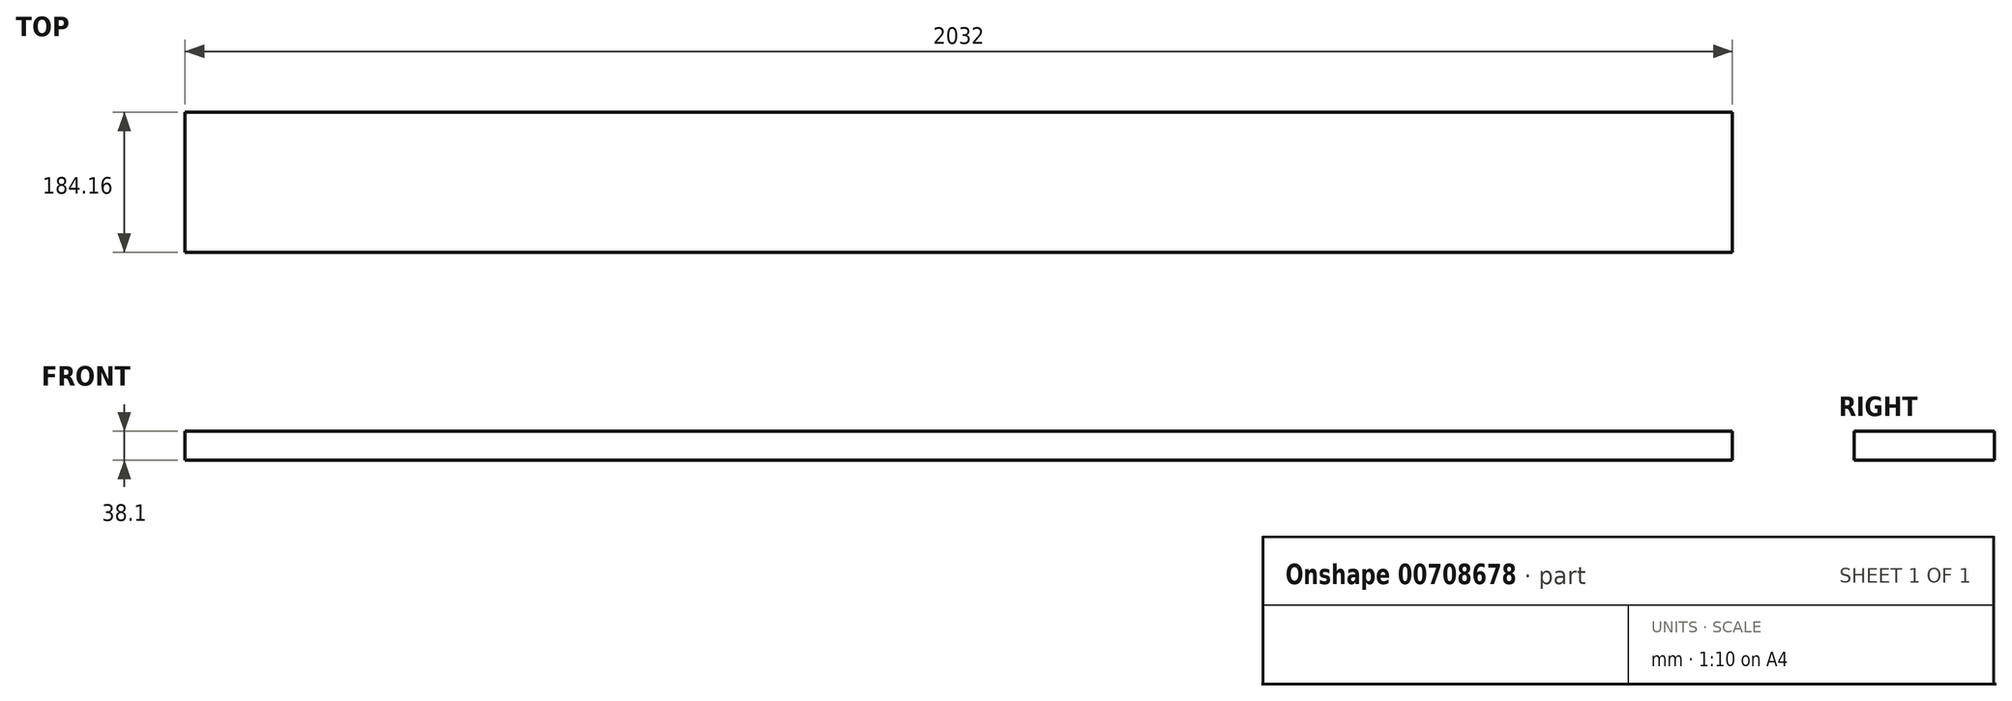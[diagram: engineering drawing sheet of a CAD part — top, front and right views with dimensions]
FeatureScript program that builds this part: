
annotation { "Feature Type Name" : "Feature", "Feature Type Description" : "" }
export const myFeature = defineFeature(function(context is Context, id is Id, definition is map)
    precondition{}
    {
        {
            var Q0;
            Q0=qCreatedBy(makeId("Right.planeOp"),FACE);
            var sketch = newSketch(context, id + "F0", { "sketchPlane" : qUnion([Q0])});
            skLineSegment(sketch, "E0.bottom", {"start": v(92.07, -19.05) * mm, "end": v(-92.07, -19.05) * mm});
            skLineSegment(sketch, "E0.top", {"start": v(92.07, 19.05) * mm, "end": v(-92.07, 19.05) * mm});
            skLineSegment(sketch, "E0.left", {"start": v(92.07, -19.05) * mm, "end": v(92.07, 19.05) * mm});
            skLineSegment(sketch, "E0.right", {"start": v(-92.07, -19.05) * mm, "end": v(-92.07, 19.05) * mm});
            skPoint(sketch, "E0.middle", {"position": v(0, 0) * mm});
            skSolve(sketch);
        }
        {
            var Q0;
            Q0=makeQuery(id+"F0.imprint","IMPRINT",FACE,{"disambiguationData":[TD([[makeQuery(id+"F0.imprint","IMPRINT",EDGE,{"derivedFrom":sQuery(id+"F0.wireOp",EDGE,"E0.bottom")}),-1.0]])]});
            extrude(context, id + "F1", {"entities" : qUnion([Q0]), "endBound" : BoundingType.SYMMETRIC, "depth" : 2032 * mm, "offsetDistance" : 25.4 * mm});
        }
    });
